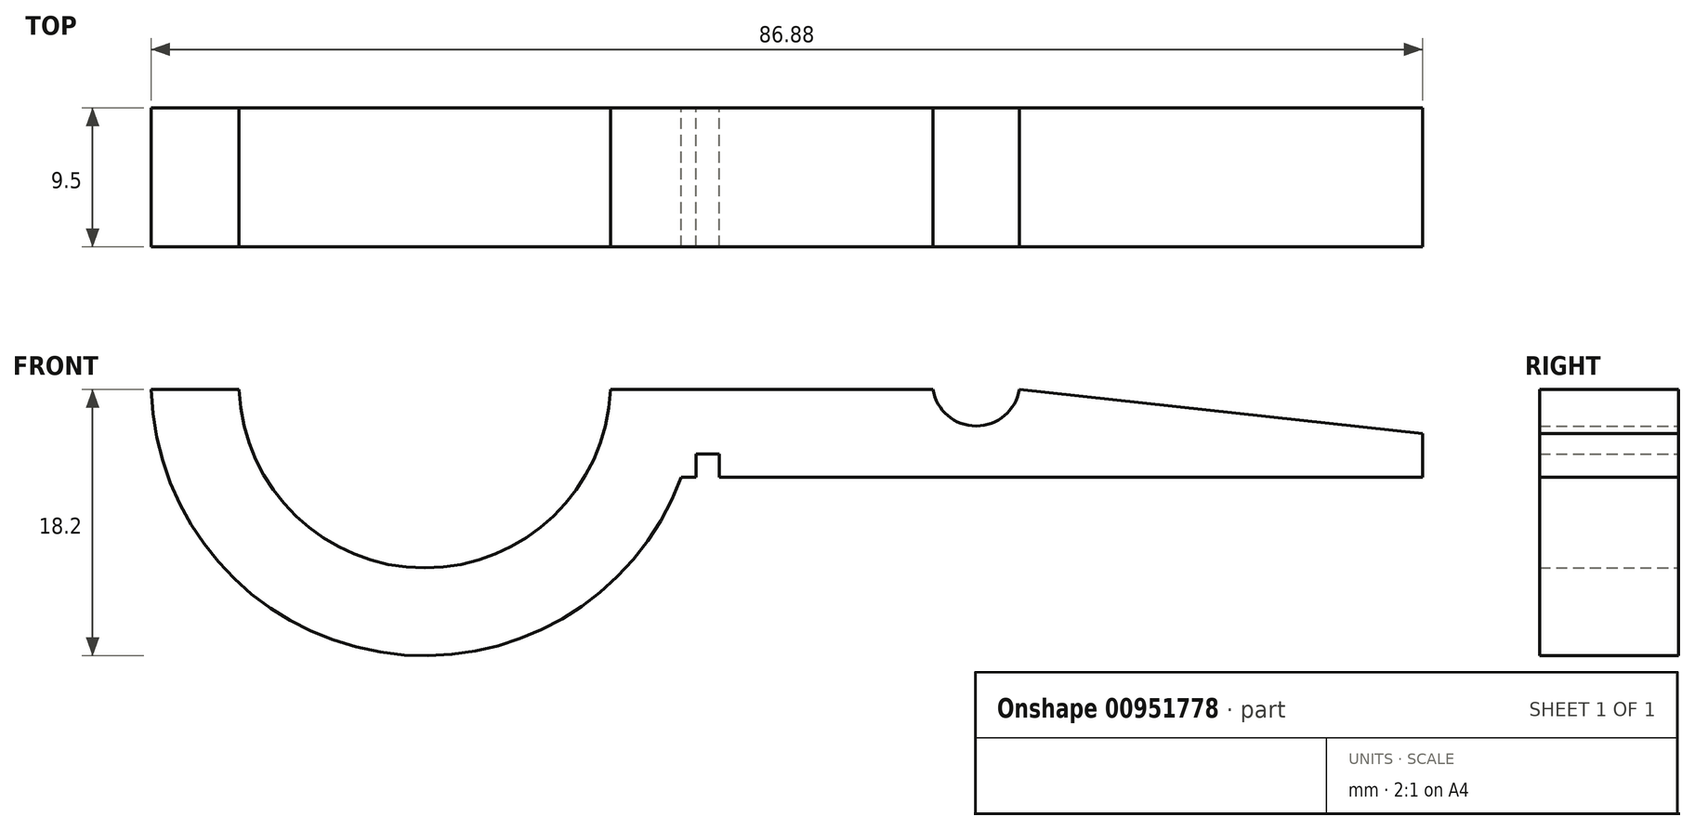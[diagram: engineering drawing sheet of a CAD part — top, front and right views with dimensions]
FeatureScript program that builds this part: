
annotation { "Feature Type Name" : "Feature", "Feature Type Description" : "" }
export const myFeature = defineFeature(function(context is Context, id is Id, definition is map)
    precondition{}
    {
        {
            assignVariable(context, id + "F0", {"name" : "springwidth", "anyValue" : 12});
        }
        {
            var Q0;
            Q0=qCreatedBy(makeId("Front.planeOp"),FACE);
            var sketch = newSketch(context, id + "F1", { "sketchPlane" : qUnion([Q0])});
            skLineSegment(sketch, "E0.right", {"start": v(30.5, -6.5) * mm, "end": v(30.5, -3.5) * mm});
            skLineSegment(sketch, "E1", {"start": v(2.96, -0.5) * mm, "end": v(30.5, -3.5) * mm});
            skLineSegment(sketch, "E2.trimOffspring", {"start": v(-25, -0.5) * mm, "end": v(-17.18, -0.5) * mm});
            skPoint(sketch, "E3.center.orphan", {"position": v(0, 0) * mm});
            skArc(sketch, "E4", {"start": v(-2.96, -0.5) * mm, "mid": v(0, -3) * mm, "end": v(2.96, -0.5) * mm});
            skLineSegment(sketch, "E5.top", {"start": v(-19.16, -4.9) * mm, "end": v(-17.56, -4.9) * mm});
            skLineSegment(sketch, "E5.left", {"start": v(-19.16, -6.5) * mm, "end": v(-19.16, -4.9) * mm});
            skLineSegment(sketch, "E5.right", {"start": v(-17.56, -6.5) * mm, "end": v(-17.56, -4.9) * mm});
            skLineSegment(sketch, "E6.trimOffspring", {"start": v(-17.56, -6.5) * mm, "end": v(30.5, -6.5) * mm});
            skPoint(sketch, "E7", {"position": v(-18.36, -4.9) * mm});
            skLineSegment(sketch, "E8", {"start": v(-2.96, -0.5) * mm, "end": v(2.96, -0.5) * mm, "construction": true});
            skArc(sketch, "E9", {"start": v(-50.38, -0.5) * mm, "mid": v(-37.7, -12.7) * mm, "end": v(-25, -0.5) * mm});
            skLineSegment(sketch, "E10", {"start": v(-17.18, -0.5) * mm, "end": v(-17.16, -0.5) * mm});
            skArc(sketch, "E11", {"start": v(-56.38, -0.5) * mm, "mid": v(-40.75, -18.45) * mm, "end": v(-20.16, -6.5) * mm});
            skLineSegment(sketch, "E12", {"start": v(-19, -0.5) * mm, "end": v(-19, -0.5) * mm});
            skLineSegment(sketch, "E13", {"start": v(-17.16, -0.5) * mm, "end": v(-2.96, -0.5) * mm});
            skLineSegment(sketch, "E14", {"start": v(-20.16, -6.5) * mm, "end": v(-19.16, -6.5) * mm});
            skLineSegment(sketch, "E15", {"start": v(-56.38, -0.5) * mm, "end": v(-50.38, -0.5) * mm});
            skSolve(sketch);
        }
        {
            var Q0;
            Q0=makeQuery(id+"F1.imprint","IMPRINT",FACE,{"disambiguationData":[TD([[makeQuery(id+"F1.imprint","IMPRINT",EDGE,{"derivedFrom":sQuery(id+"F1.wireOp",EDGE,"E0.right")}),1.0]])]});
            extrude(context, id + "F2", {"entities" : qUnion([Q0]), "offsetDistance" : 25 * mm, "depth" : (getVariable(context, 'springwidth') - 2.5) * mm});
        }
    });
